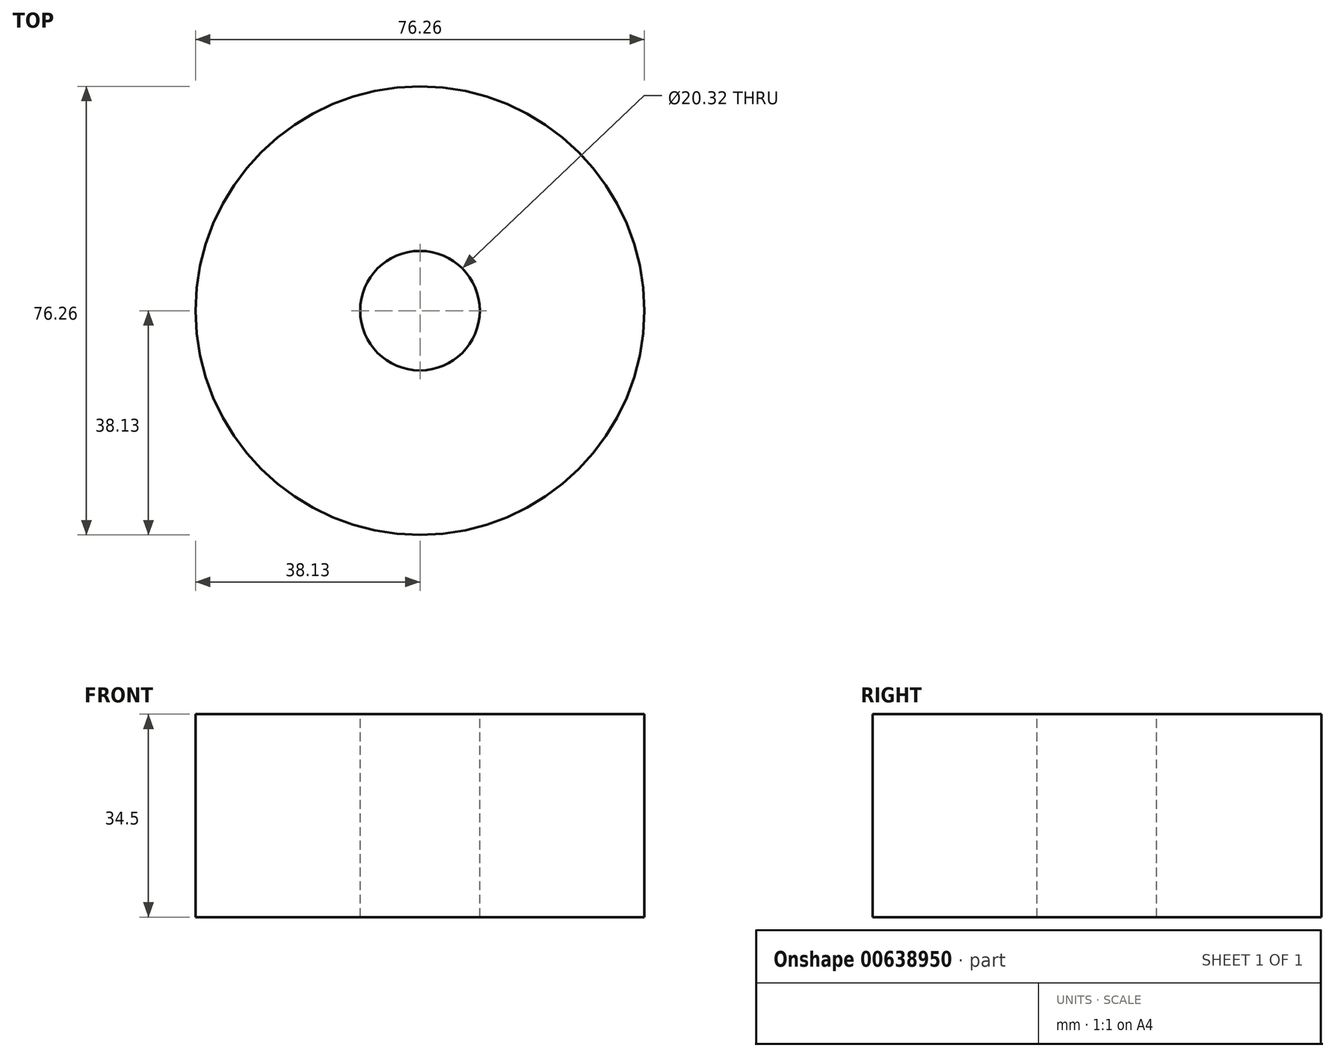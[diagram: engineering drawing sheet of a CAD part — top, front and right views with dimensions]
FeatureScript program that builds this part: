
annotation { "Feature Type Name" : "Feature", "Feature Type Description" : "" }
export const myFeature = defineFeature(function(context is Context, id is Id, definition is map)
    precondition{}
    {
        {
            var Q0;
            Q0=qCreatedBy(makeId("Top.planeOp"),FACE);
            var sketch = newSketch(context, id + "F0", { "sketchPlane" : qUnion([Q0])});
            skCircle(sketch, "E0", {"center": v(0, 0) * mm, "radius": 38.13 * mm});
            skSolve(sketch);
        }
        {
            var Q0;
            Q0=makeQuery(id+"F0.imprint","IMPRINT",FACE,{"disambiguationData":[TD([[makeQuery(id+"F0.imprint","IMPRINT",EDGE,{"derivedFrom":sQuery(id+"F0.wireOp",EDGE,"E0")}),1.0]])]});
            extrude(context, id + "F1", {"entities" : qUnion([Q0]), "depth" : 34.5 * mm, "offsetDistance" : 25 * mm});
        }
        {
            var Q0;
            Q0=makeQuery(id+"F1.opExtrude","CAP_FACE",FACE,{"disambiguationData":[OSD([sQuery(id+"F0.wireOp",EDGE,"E0")])],"isStart":false});
            var sketch = newSketch(context, id + "F2", { "sketchPlane" : qUnion([Q0])});
            skCircle(sketch, "E1", {"center": v(0, 0) * mm, "radius": 10.16 * mm});
            skSolve(sketch);
        }
        {
            var Q0;
            Q0=makeQuery(id+"F2.imprint","IMPRINT",FACE,{"disambiguationData":[TD([[makeQuery(id+"F2.imprint","IMPRINT",EDGE,{"derivedFrom":sQuery(id+"F2.wireOp",EDGE,"E1")}),1.0]])]});
            var Q1;
            Q1=sQuery(id+"F2.wireOp",EDGE,"E1");
            extrude(context, id + "F3", {"entities" : qUnion([Q0]), "operationType" : NewBodyOperationType.REMOVE, "surfaceEntities" : qUnion([Q1]), "oppositeDirection" : true, "depth" : 92 * mm, "offsetDistance" : 25 * mm});
        }
    });
